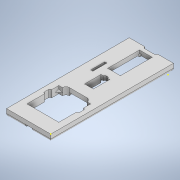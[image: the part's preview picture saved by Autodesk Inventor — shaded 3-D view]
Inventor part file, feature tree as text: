
AUTODESK INVENTOR PART (.ipt)
format: ipt  version: 2022 (Build 260153000, 153)  size: 329,728 bytes
history: native  units: mm
features: chamfer x8, sketch x6, extrude x4, fillet x1, plane x1
ambient origin geometry x8: Origin, YZ Plane, XZ Plane, XY Plane, X Axis, Y Axis, Z Axis, Center Point
bodies: Solid1 (feature_tree)
feature tree (20):
  extrude  "Extrusion1"  Depth=62.5mm
  extrude  "Extrusion2"  Depth=10.0mm
  sketch  "Sketch3"  dims[d5=6.2mm d6=6.2mm d7=16.9mm]
  extrude  "Extrusion3"  Depth=6.2mm
  sketch  "Sketch5"  dims[d11=20.25mm]
  fillet  "Fillet1"  Radius=16.9mm
  plane  "Work Plane1"
  extrude  "Extrusion4"  Depth=9.0mm TaperAngle=0.0deg
  chamfer  "Chamfer1"  Distance=45.0mm
  chamfer  "Chamfer2"  Distance=18.0mm
  chamfer  "Chamfer3"  Distance=6.0mm
  chamfer  "Chamfer4"  Distance=4.0mm
  chamfer  "Chamfer5"  Distance=3.0mm
  chamfer  "Chamfer6"  Distance=20.0mm
  chamfer  "Chamfer7"  Distance=3.0mm
  chamfer  "Chamfer8"  Distance=22.5mm
  sketch  "Sketch1"  dims[d0=173.4mm d1=62.5mm]
  sketch  "Sketch2"  dims[d2=10.0mm d3=0.0mm d4=102.12mm]
  sketch  "Sketch4"  dims[d8=6.3mm d9=9.0mm d10=0.0mm]
  sketch  "Sketch6"  dims[d12=9.0mm d13=45.0mm d14=18.0mm d15=6.0mm d16=4.0mm d17=3.0mm d18=20.0mm d19=3.0mm d20=22.5mm d21=22.5mm d22=22.5mm d23=45.0mm d24=5.0mm d25=5.0mm d26=5.0mm d27=10.0mm d28=10.0mm d29=5.0mm d30=5.0mm d31=5.0mm d32=10.0mm d33=7.0mm d34=4.0mm d35=0.0mm d36=5.0mm d37=4.0mm d38=4.0mm d39=4.0mm d40=5.0mm d41=5.0mm d42=5.0mm d43=2.5mm d44=2.5mm d45=2.5mm d46=2.5mm d47=2.0mm d48=0.0mm d49=3.535mm d50=2.0mm d51=45.0deg d52=3.535mm d53=2.0mm d54=45.0deg d55=3.535mm d56=2.0mm d57=45.0deg d58=3.535mm d59=2.0mm d60=45.0deg d61=2.5mm d62=2.0mm d63=45.0deg d64=2.5mm d65=2.0mm d66=45.0deg d67=2.5mm d68=2.0mm d69=45.0deg d70=2.5mm d71=2.0mm d72=45.0deg]
